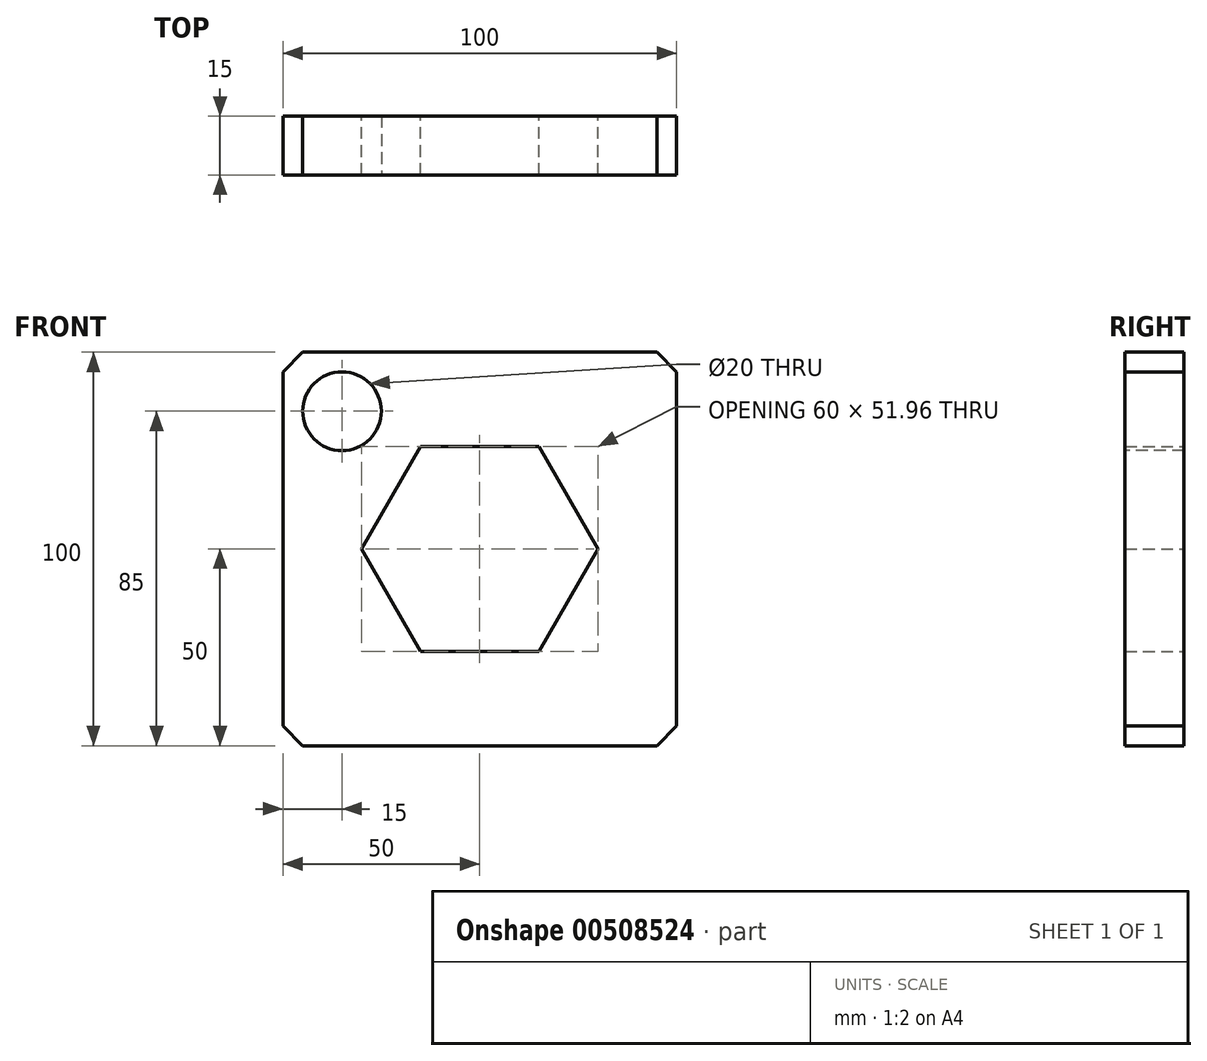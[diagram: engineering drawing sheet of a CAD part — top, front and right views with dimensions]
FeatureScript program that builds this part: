
annotation { "Feature Type Name" : "Feature", "Feature Type Description" : "" }
export const myFeature = defineFeature(function(context is Context, id is Id, definition is map)
    precondition{}
    {
        {
            var Q0;
            Q0=qCreatedBy(makeId("Front.planeOp"),FACE);
            var sketch = newSketch(context, id + "F0", { "sketchPlane" : qUnion([Q0])});
            skLineSegment(sketch, "E0.bottom", {"start": v(50, 50) * mm, "end": v(-50, 50) * mm});
            skLineSegment(sketch, "E0.top", {"start": v(50, -50) * mm, "end": v(-50, -50) * mm});
            skLineSegment(sketch, "E0.left", {"start": v(50, 50) * mm, "end": v(50, -50) * mm});
            skLineSegment(sketch, "E0.right", {"start": v(-50, 50) * mm, "end": v(-50, -50) * mm});
            skPoint(sketch, "E0.middle", {"position": v(0, 0) * mm});
            skLineSegment(sketch, "E1.0", {"start": v(30, 0) * mm, "end": v(15, -25.98) * mm});
            skLineSegment(sketch, "E1.1", {"start": v(15, -25.98) * mm, "end": v(-15, -25.98) * mm});
            skLineSegment(sketch, "E1.2", {"start": v(-15, -25.98) * mm, "end": v(-30, 0) * mm});
            skLineSegment(sketch, "E1.3", {"start": v(-30, 0) * mm, "end": v(-15, 25.98) * mm});
            skLineSegment(sketch, "E1.4", {"start": v(-15, 25.98) * mm, "end": v(15, 25.98) * mm});
            skLineSegment(sketch, "E1.5", {"start": v(15, 25.98) * mm, "end": v(30, 0) * mm});
            skSolve(sketch);
        }
        {
            var Q0;
            Q0 = qSketchRegion(id + "F0", true);
            extrude(context, id + "F1", {"entities" : qUnion([Q0]), "depth" : 15 * mm});
        }
        {
            var Q0;
            Q0=makeQuery(id+"F1.opExtrude","CAP_FACE",FACE,{"disambiguationData":[OSD([sQuery(id+"F0.wireOp",EDGE,"E0.bottom"),sQuery(id+"F0.wireOp",EDGE,"E0.top"),sQuery(id+"F0.wireOp",EDGE,"E0.left"),sQuery(id+"F0.wireOp",EDGE,"E0.right"),sQuery(id+"F0.wireOp",EDGE,"E1.0"),sQuery(id+"F0.wireOp",EDGE,"E1.1"),sQuery(id+"F0.wireOp",EDGE,"E1.2"),sQuery(id+"F0.wireOp",EDGE,"E1.3"),sQuery(id+"F0.wireOp",EDGE,"E1.4"),sQuery(id+"F0.wireOp",EDGE,"E1.5")])],"isStart":false});
            var sketch = newSketch(context, id + "F2", { "sketchPlane" : qUnion([Q0])});
            skCircle(sketch, "E2", {"center": v(-35, 35) * mm, "radius": 10 * mm});
            skSolve(sketch);
        }
        {
            var Q0;
            Q0=makeQuery(id+"F2.imprint","IMPRINT",FACE,{"disambiguationData":[TD([[makeQuery(id+"F2.imprint","IMPRINT",EDGE,{"derivedFrom":sQuery(id+"F2.wireOp",EDGE,"E2")}),1.0]])]});
            extrude(context, id + "F3", {"entities" : qUnion([Q0]), "operationType" : NewBodyOperationType.REMOVE, "endBound" : BoundingType.THROUGH_ALL, "oppositeDirection" : true, "depth" : 25 * mm});
        }
        {
            var Q0;
            Q0=makeQuery(id+"F1.opExtrude","SWEPT_EDGE",EDGE,{"disambiguationData":[OSD([sQuery(id+"F0.wireOp",EDGE,"E0.bottom"),sQuery(id+"F0.wireOp",EDGE,"E0.left")])]});
            var Q1;
            Q1=makeQuery(id+"F1.opExtrude","SWEPT_EDGE",EDGE,{"disambiguationData":[OSD([sQuery(id+"F0.wireOp",EDGE,"E0.bottom"),sQuery(id+"F0.wireOp",EDGE,"E0.right")])]});
            var Q2;
            Q2=makeQuery(id+"F1.opExtrude","SWEPT_EDGE",EDGE,{"disambiguationData":[OSD([sQuery(id+"F0.wireOp",EDGE,"E0.top"),sQuery(id+"F0.wireOp",EDGE,"E0.left")])]});
            var Q3;
            Q3=makeQuery(id+"F1.opExtrude","SWEPT_EDGE",EDGE,{"disambiguationData":[OSD([sQuery(id+"F0.wireOp",EDGE,"E0.top"),sQuery(id+"F0.wireOp",EDGE,"E0.right")])]});
            chamfer(context, id + "F4", {"entities" : qUnion([Q0, Q1, Q2, Q3]), "width" : 5 * mm, "tangentPropagation" : true});
        }
    });
